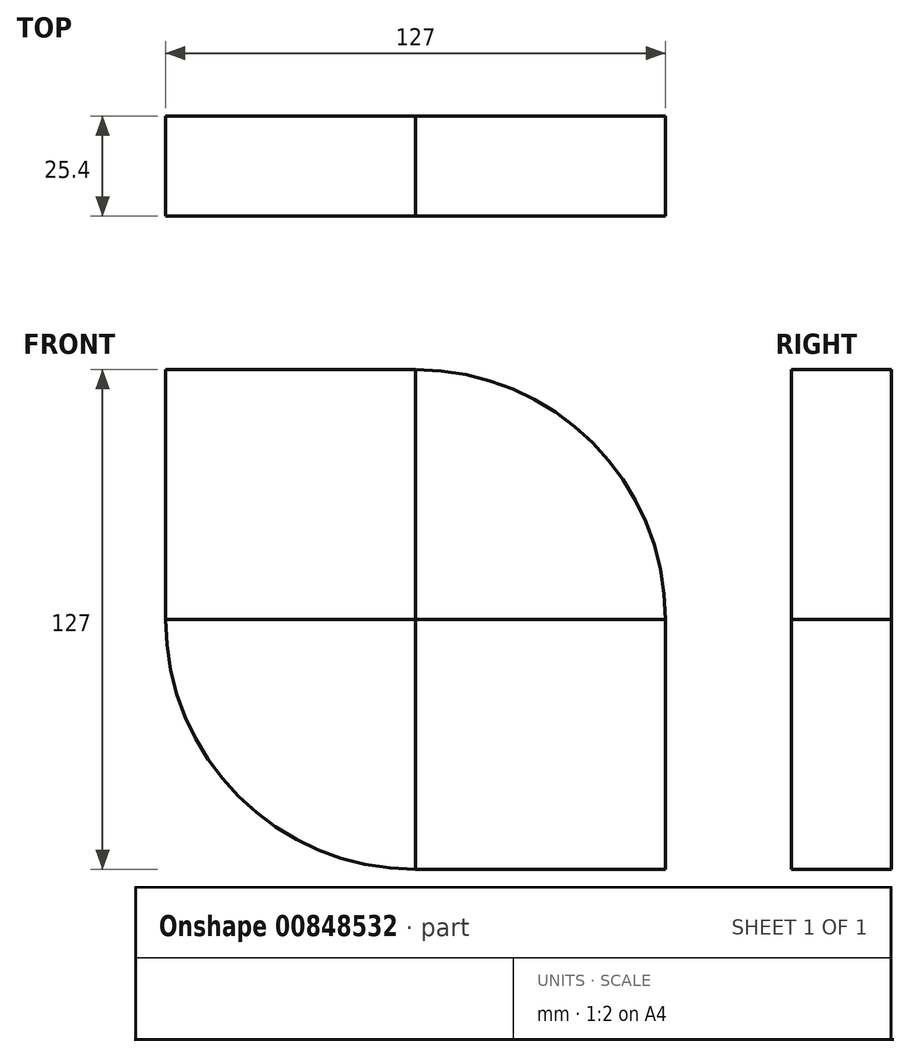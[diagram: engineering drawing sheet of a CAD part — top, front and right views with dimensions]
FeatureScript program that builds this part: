
annotation { "Feature Type Name" : "Feature", "Feature Type Description" : "" }
export const myFeature = defineFeature(function(context is Context, id is Id, definition is map)
    precondition{}
    {
        {
            var Q0;
            Q0=qCreatedBy(makeId("Front.planeOp"),FACE);
            var sketch = newSketch(context, id + "F0", { "sketchPlane" : qUnion([Q0])});
            skCircle(sketch, "E0", {"center": v(0, 0) * mm, "radius": 63.5 * mm});
            skLineSegment(sketch, "E1", {"start": v(0, 0) * mm, "end": v(0, 63.5) * mm});
            skLineSegment(sketch, "E2", {"start": v(0, 0) * mm, "end": v(0, -63.5) * mm});
            skLineSegment(sketch, "E3", {"start": v(0, 0) * mm, "end": v(-63.5, 0) * mm});
            skLineSegment(sketch, "E4", {"start": v(0, 0) * mm, "end": v(63.5, 0) * mm});
            skLineSegment(sketch, "E5", {"start": v(-63.5, 0) * mm, "end": v(0, 63.5) * mm});
            skLineSegment(sketch, "E6", {"start": v(-63.5, 0) * mm, "end": v(-63.5, 63.5) * mm});
            skLineSegment(sketch, "E7", {"start": v(-63.5, 63.5) * mm, "end": v(0, 63.5) * mm});
            skLineSegment(sketch, "E8", {"start": v(63.5, 0) * mm, "end": v(0, -63.5) * mm});
            skLineSegment(sketch, "E9", {"start": v(0, -63.5) * mm, "end": v(63.5, -63.5) * mm});
            skLineSegment(sketch, "E10", {"start": v(63.5, -63.5) * mm, "end": v(63.5, 0) * mm});
            skSolve(sketch);
        }
        {
            var Q0;
            {var subQ0=sQuery(id+"F0.wireOp",EDGE,"E2");Q0=makeQuery(id+"F0.imprint","IMPRINT",FACE,{"disambiguationData":[TD([[makeQuery(id+"F0.imprint","IMPRINT",EDGE,{"derivedFrom":subQ0}),-1.0]])]});}
            var Q1;
            {var subQ0=sQuery(id+"F0.wireOp",EDGE,"E1");Q1=makeQuery(id+"F0.imprint","IMPRINT",FACE,{"disambiguationData":[TD([[makeQuery(id+"F0.imprint","IMPRINT",EDGE,{"derivedFrom":subQ0}),-1.0]])]});}
            extrude(context, id + "F1", {"entities" : qUnion([Q0, Q1]), "depth" : 25.4 * mm, "offsetDistance" : 25.4 * mm});
        }
        {
            var Q0;
            {var subQ3=sQuery(id+"F0.wireOp",EDGE,"E6");Q0=makeQuery(id+"F0.imprint","IMPRINT",FACE,{"disambiguationData":[TD([[makeQuery(id+"F0.imprint","IMPRINT",EDGE,{"derivedFrom":subQ3}),-1.0]])]});}
            var Q1;
            {var subQ0=sQuery(id+"F0.wireOp",EDGE,"E5");Q1=makeQuery(id+"F0.imprint","IMPRINT",FACE,{"disambiguationData":[TD([[makeQuery(id+"F0.imprint","IMPRINT",EDGE,{"derivedFrom":subQ0}),1.0]])]});}
            var Q2;
            Q2=makeQuery(id+"F0.imprint","IMPRINT",FACE,{"disambiguationData":[TD([[makeQuery(id+"F0.imprint","IMPRINT",EDGE,{"derivedFrom":sQuery(id+"F0.wireOp",EDGE,"E1")}),1.0]])]});
            var Q3;
            {var subQ0=sQuery(id+"F0.wireOp",EDGE,"E8");Q3=makeQuery(id+"F0.imprint","IMPRINT",FACE,{"disambiguationData":[TD([[makeQuery(id+"F0.imprint","IMPRINT",EDGE,{"derivedFrom":subQ0}),1.0]])]});}
            var Q4;
            Q4=makeQuery(id+"F0.imprint","IMPRINT",FACE,{"disambiguationData":[TD([[makeQuery(id+"F0.imprint","IMPRINT",EDGE,{"derivedFrom":sQuery(id+"F0.wireOp",EDGE,"E2")}),1.0]])]});
            var Q5;
            {var subQ0=sQuery(id+"F0.wireOp",EDGE,"E9");Q5=makeQuery(id+"F0.imprint","IMPRINT",FACE,{"disambiguationData":[TD([[makeQuery(id+"F0.imprint","IMPRINT",EDGE,{"derivedFrom":subQ0}),1.0]])]});}
            extrude(context, id + "F2", {"entities" : qUnion([Q0, Q1, Q2, Q3, Q4, Q5]), "depth" : 25.4 * mm, "offsetDistance" : 25.4 * mm});
        }
    });
